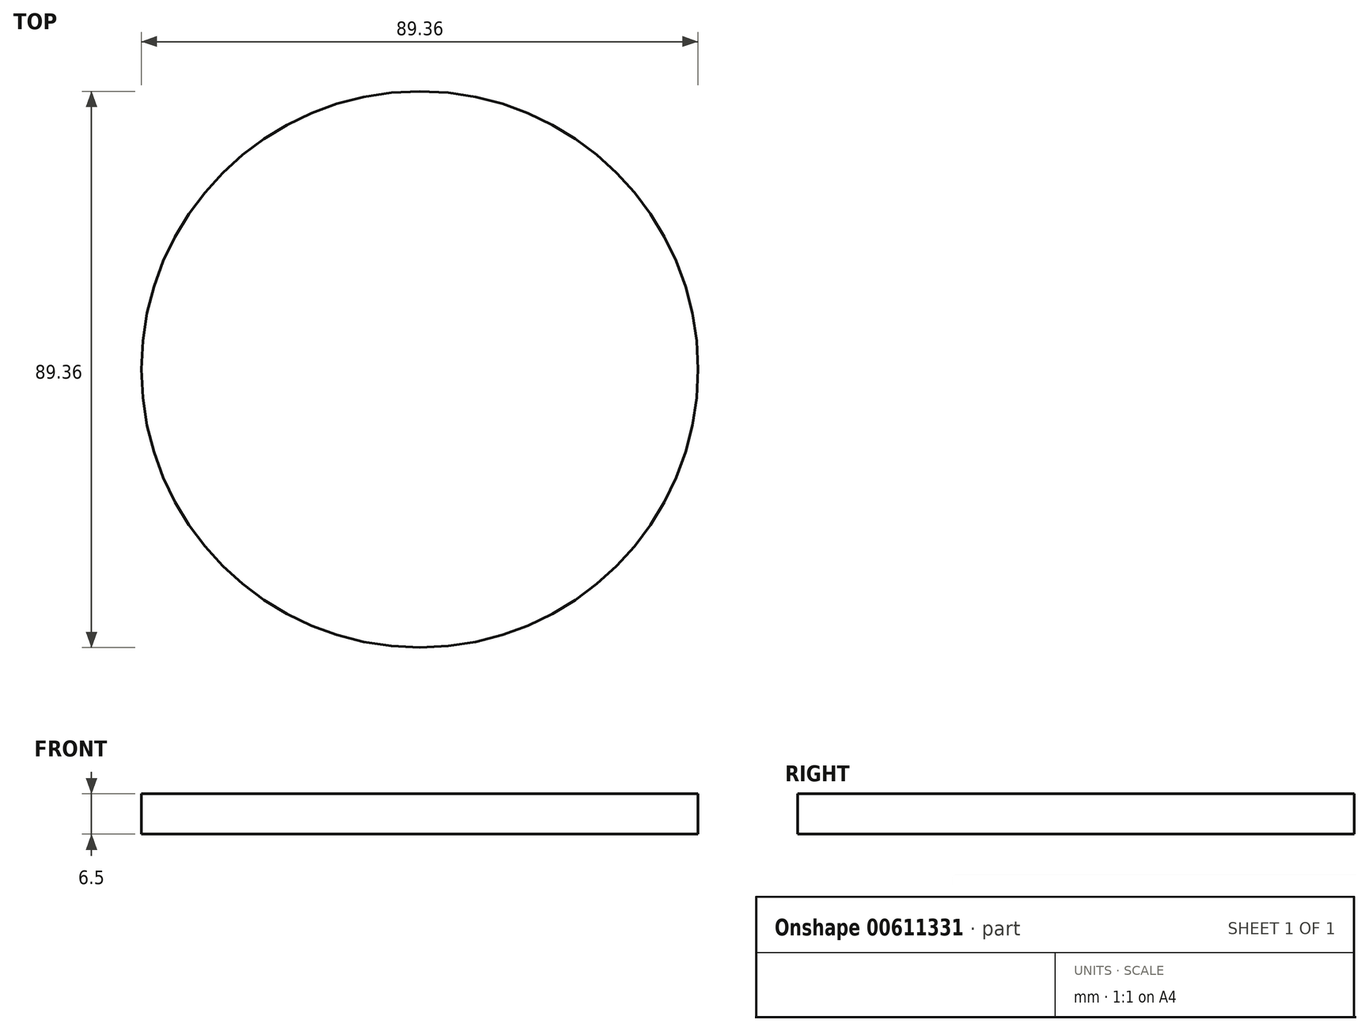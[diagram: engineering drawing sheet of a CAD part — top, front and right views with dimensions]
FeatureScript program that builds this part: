
annotation { "Feature Type Name" : "Feature", "Feature Type Description" : "" }
export const myFeature = defineFeature(function(context is Context, id is Id, definition is map)
    precondition{}
    {
        {
            var Q0;
            Q0=qCreatedBy(makeId("Top.planeOp"),FACE);
            var sketch = newSketch(context, id + "F0", { "sketchPlane" : qUnion([Q0])});
            skCircle(sketch, "E0", {"center": v(0, 0) * mm, "radius": 44.68 * mm});
            skSolve(sketch);
        }
        {
            var Q0;
            Q0 = qSketchRegion(id + "F0", true);
            extrude(context, id + "F1", {"entities" : qUnion([Q0]), "depth" : 6.5 * mm, "offsetDistance" : 25 * mm});
        }
    });
